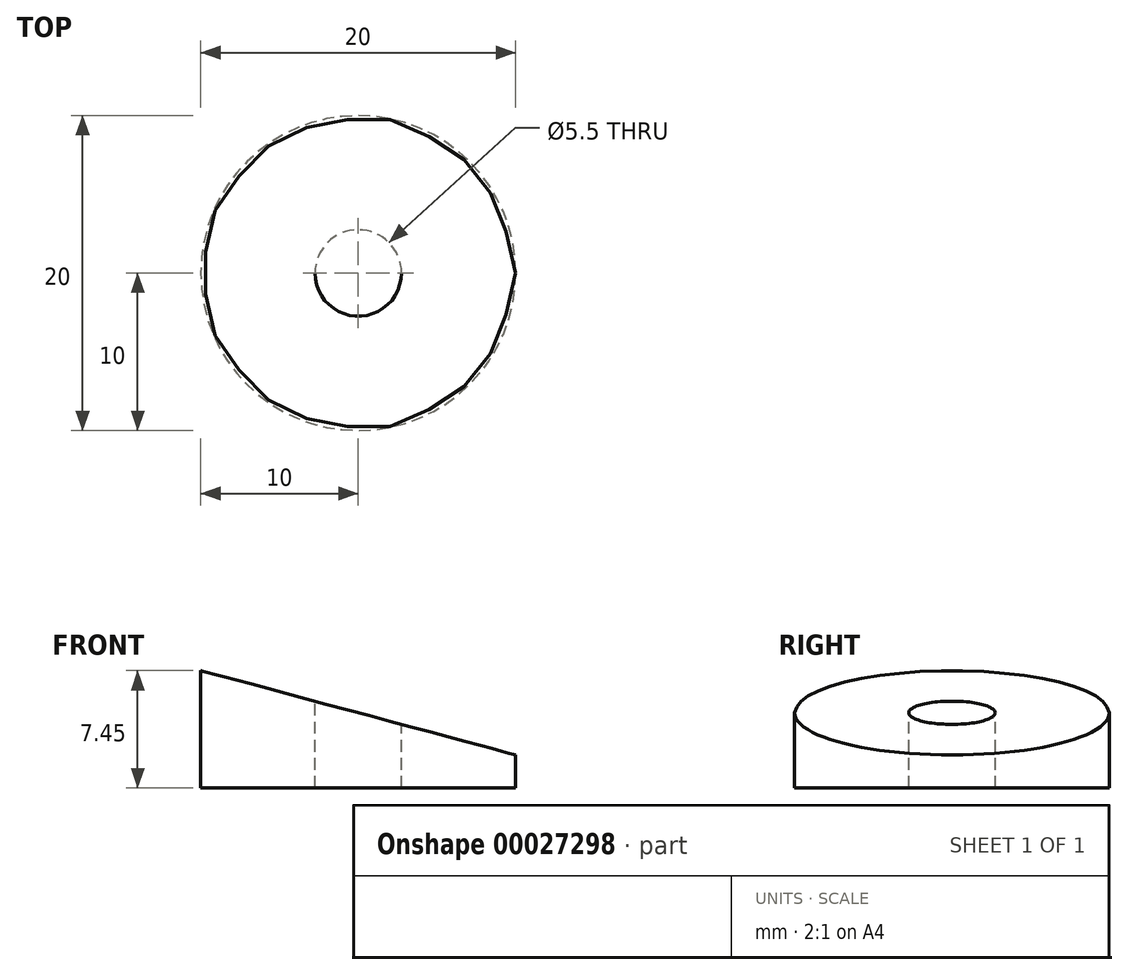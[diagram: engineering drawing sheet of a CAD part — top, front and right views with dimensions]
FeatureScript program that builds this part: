
annotation { "Feature Type Name" : "Feature", "Feature Type Description" : "" }
export const myFeature = defineFeature(function(context is Context, id is Id, definition is map)
    precondition{}
    {
        {
            var Q0;
            Q0=qCreatedBy(makeId("Top.planeOp"),FACE);
            var sketch = newSketch(context, id + "F0", { "sketchPlane" : qUnion([Q0])});
            skCircle(sketch, "E0", {"center": v(0, 0) * mm, "radius": 10 * mm});
            skSolve(sketch);
        }
        {
            var Q0;
            Q0 = qSketchRegion(id + "F0", true);
            extrude(context, id + "F1", {"entities" : qUnion([Q0]), "depth" : 38 * mm, "offsetDistance" : 25 * mm});
        }
        {
            var Q0;
            Q0=makeQuery(id+"F1.opExtrude","CAP_FACE",FACE,{"disambiguationData":[OSD([sQuery(id+"F0.wireOp",EDGE,"E0")])],"isStart":true});
            var sketch = newSketch(context, id + "F2", { "sketchPlane" : qUnion([Q0])});
            skCircle(sketch, "E1", {"center": v(0, 0) * mm, "radius": 6.4 * mm});
            skSolve(sketch);
        }
        {
            var Q0;
            Q0 = qSketchRegion(id + "F2", true);
            extrude(context, id + "F3", {"entities" : qUnion([Q0]), "operationType" : NewBodyOperationType.REMOVE, "oppositeDirection" : true, "depth" : 9.2 * mm, "offsetDistance" : 25 * mm});
        }
        {
            var Q0;
            Q0=makeQuery(id+"F1.opExtrude","CAP_FACE",FACE,{"disambiguationData":[OSD([sQuery(id+"F0.wireOp",EDGE,"E0")])],"isStart":false});
            var sketch = newSketch(context, id + "F4", { "sketchPlane" : qUnion([Q0])});
            skCircle(sketch, "E2", {"center": v(0, 0) * mm, "radius": 2.75 * mm});
            skSolve(sketch);
        }
        {
            var Q0;
            Q0 = qSketchRegion(id + "F4", true);
            extrude(context, id + "F5", {"entities" : qUnion([Q0]), "operationType" : NewBodyOperationType.REMOVE, "endBound" : BoundingType.THROUGH_ALL, "oppositeDirection" : true, "depth" : 25 * mm, "offsetDistance" : 25 * mm});
        }
        {
            var Q0;
            Q0=qCreatedBy(makeId("Front.planeOp"),FACE);
            var sketch = newSketch(context, id + "F6", { "sketchPlane" : qUnion([Q0])});
            skLineSegment(sketch, "E3", {"start": v(-18.57, 40.05) * mm, "end": v(12.5, 40.05) * mm});
            skLineSegment(sketch, "E4", {"start": v(-18.57, 40.05) * mm, "end": v(13.63, 31.42) * mm});
            skLineSegment(sketch, "E5", {"start": v(12.5, 40.05) * mm, "end": v(13.63, 31.42) * mm});
            skSolve(sketch);
        }
        {
            var Q0;
            Q0 = qSketchRegion(id + "F6", true);
            extrude(context, id + "F7", {"entities" : qUnion([Q0]), "operationType" : NewBodyOperationType.REMOVE, "endBound" : BoundingType.SYMMETRIC, "oppositeDirection" : true, "depth" : 25 * mm, "offsetDistance" : 25 * mm});
        }
        {
            var Q0;
            Q0=qCreatedBy(makeId("Front.planeOp"),FACE);
            var sketch = newSketch(context, id + "F8", { "sketchPlane" : qUnion([Q0])});
            skLineSegment(sketch, "E6.bottom", {"start": v(-17.2, 30.3) * mm, "end": v(20.99, 30.3) * mm});
            skLineSegment(sketch, "E6.top", {"start": v(-17.2, -8.13) * mm, "end": v(20.99, -8.13) * mm});
            skLineSegment(sketch, "E6.left", {"start": v(-17.2, 30.3) * mm, "end": v(-17.2, -8.13) * mm});
            skLineSegment(sketch, "E6.right", {"start": v(20.99, 30.3) * mm, "end": v(20.99, -8.13) * mm});
            skSolve(sketch);
        }
        {
            var Q0;
            Q0 = qSketchRegion(id + "F8", true);
            extrude(context, id + "F9", {"entities" : qUnion([Q0]), "operationType" : NewBodyOperationType.REMOVE, "endBound" : BoundingType.SYMMETRIC, "depth" : 25 * mm, "offsetDistance" : 25 * mm});
        }
    });
